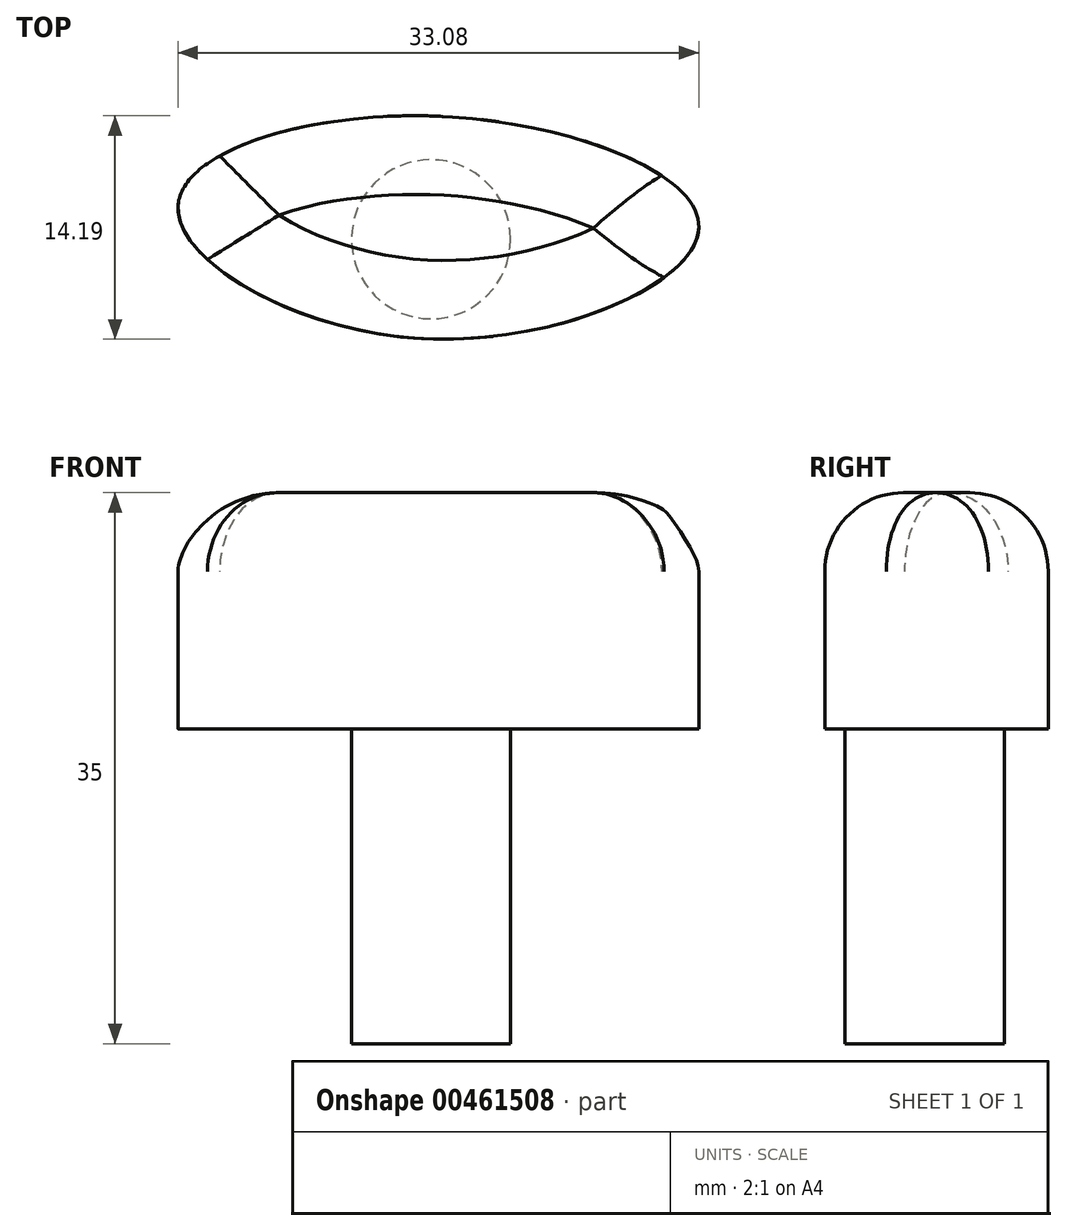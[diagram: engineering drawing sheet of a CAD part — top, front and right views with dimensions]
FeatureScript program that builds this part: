
annotation { "Feature Type Name" : "Feature", "Feature Type Description" : "" }
export const myFeature = defineFeature(function(context is Context, id is Id, definition is map)
    precondition{}
    {
        {
            var Q0;
            Q0=qCreatedBy(makeId("Top.planeOp"),FACE);
            var sketch = newSketch(context, id + "F0", { "sketchPlane" : qUnion([Q0])});
            skFitSpline(sketch, "E0", {"points": [v(-21.2, -1.67) * mm, v(-5.65, -10.15) * mm, v(11.88, -3.08) * mm, v(-4.8, 3.99) * mm, v(-21.2, -1.67) * mm]});
            skSolve(sketch);
        }
        {
            var Q0;
            Q0=makeQuery(id+"F0.imprint","IMPRINT",FACE,{"disambiguationData":[TD([[makeQuery(id+"F0.imprint","IMPRINT",EDGE,{"derivedFrom":sQuery(id+"F0.wireOp",EDGE,"E0")}),1.0]])]});
            extrude(context, id + "F1", {"entities" : qUnion([Q0]), "depth" : 15 * mm});
        }
        {
            var Q0;
            Q0=makeQuery(id+"F1.opExtrude","CAP_EDGE",EDGE,{"disambiguationData":[OSD([sQuery(id+"F0.wireOp",EDGE,"E0")])],"isStart":false});
            fillet(context, id + "F2", {"entities" : qUnion([Q0]), "radius" : 5 * mm, "tangentPropagation" : true, "allowEdgeOverflow" : false});
        }
        {
            var Q0;
            Q0=makeQuery(id+"F1.opExtrude","CAP_FACE",FACE,{"disambiguationData":[OSD([sQuery(id+"F0.wireOp",EDGE,"E0")])],"isStart":true});
            var sketch = newSketch(context, id + "F3", { "sketchPlane" : qUnion([Q0])});
            skCircle(sketch, "E1", {"center": v(-5.13, 3.83) * mm, "radius": 5.05 * mm});
            skSolve(sketch);
        }
        {
            var Q0;
            Q0=makeQuery(id+"F3.imprint","IMPRINT",FACE,{"disambiguationData":[TD([[makeQuery(id+"F3.imprint","IMPRINT",EDGE,{"derivedFrom":sQuery(id+"F3.wireOp",EDGE,"E1")}),1.0]])]});
            extrude(context, id + "F4", {"entities" : qUnion([Q0]), "operationType" : NewBodyOperationType.ADD, "depth" : 20 * mm});
        }
    });
